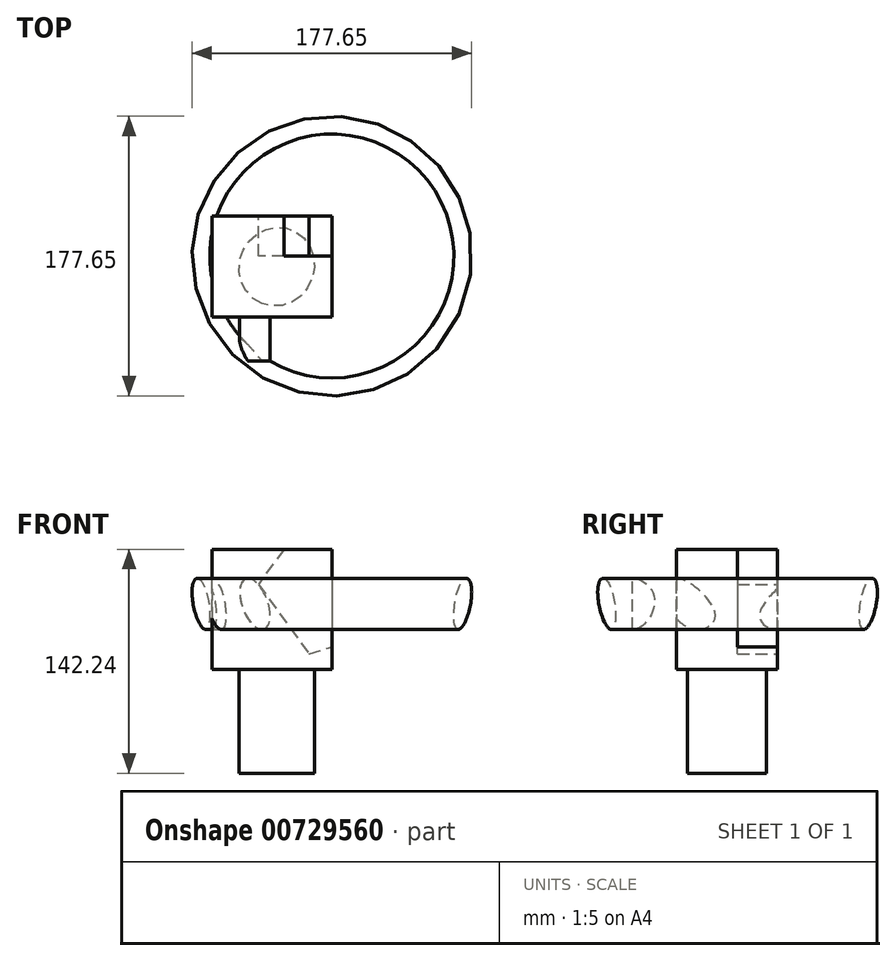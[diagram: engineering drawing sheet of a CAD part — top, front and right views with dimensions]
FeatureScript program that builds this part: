
annotation { "Feature Type Name" : "Feature", "Feature Type Description" : "" }
export const myFeature = defineFeature(function(context is Context, id is Id, definition is map)
    precondition{}
    {
        {
            var Q0;
            Q0=qCreatedBy(makeId("Front.planeOp"),FACE);
            var sketch = newSketch(context, id + "F0", { "sketchPlane" : qUnion([Q0])});
            skLineSegment(sketch, "E0", {"start": v(-41.12, 88.64) * mm, "end": v(35.08, 88.64) * mm});
            skLineSegment(sketch, "E1", {"start": v(35.08, 88.64) * mm, "end": v(35.08, 12.44) * mm});
            skLineSegment(sketch, "E2", {"start": v(35.08, 12.44) * mm, "end": v(-41.12, 12.44) * mm});
            skLineSegment(sketch, "E3", {"start": v(-41.12, 12.44) * mm, "end": v(-41.12, 88.64) * mm});
            skSolve(sketch);
        }
        {
            var Q0;
            Q0 = qSketchRegion(id + "F0", true);
            extrude(context, id + "F1", {"entities" : qUnion([Q0]), "oppositeDirection" : true, "depth" : 64.26 * mm, "offsetDistance" : 25.4 * mm});
        }
        {
            var Q0;
            Q0=makeQuery(id+"F1.opExtrude","CAP_FACE",FACE,{"disambiguationData":[OSD([sQuery(id+"F0.wireOp",EDGE,"E0"),sQuery(id+"F0.wireOp",EDGE,"E1"),sQuery(id+"F0.wireOp",EDGE,"E2"),sQuery(id+"F0.wireOp",EDGE,"E3")])],"isStart":false});
            var sketch = newSketch(context, id + "F2", { "sketchPlane" : qUnion([Q0])});
            skCircle(sketch, "E4.cCircle", {"center": v(-35.08, 66.47) * mm, "radius": 37.73 * mm, "construction": true});
            skLineSegment(sketch, "E4.0", {"start": v(-20.65, 110.82) * mm, "end": v(11.56, 66.46) * mm});
            skLineSegment(sketch, "E4.1", {"start": v(11.56, 66.46) * mm, "end": v(-20.67, 22.1) * mm});
            skLineSegment(sketch, "E4.2", {"start": v(-20.67, 22.1) * mm, "end": v(-72.81, 39.06) * mm});
            skLineSegment(sketch, "E4.3", {"start": v(-72.81, 39.06) * mm, "end": v(-72.8, 93.89) * mm});
            skLineSegment(sketch, "E4.4", {"start": v(-72.8, 93.89) * mm, "end": v(-20.65, 110.82) * mm});
            skPoint(sketch, "E4.0.midPoint", {"position": v(-4.55, 88.64) * mm});
            skSolve(sketch);
        }
        {
            var Q0;
            Q0 = qSketchRegion(id + "F2", true);
            extrude(context, id + "F3", {"entities" : qUnion([Q0]), "operationType" : NewBodyOperationType.REMOVE, "oppositeDirection" : true, "depth" : 25.4 * mm, "offsetDistance" : 25.4 * mm});
        }
        {
            var Q0;
            Q0=makeQuery(id+"F1.opExtrude","SWEPT_FACE",FACE,{"disambiguationData":[OSD([sQuery(id+"F0.wireOp",EDGE,"E2")])]});
            var sketch = newSketch(context, id + "F4", { "sketchPlane" : qUnion([Q0])});
            skEllipse(sketch, "E5", {"center": v(0, -32.13) * mm, "majorRadius": 25.18 * mm, "minorRadius": 23.75 * mm, "majorAxis": v(-0.37, 0.93)});
            skPoint(sketch, "E5.centerSnap0", {"position": v(-41.12, -32.13) * mm});
            skSolve(sketch);
        }
        {
            var Q0;
            Q0 = qSketchRegion(id + "F4", true);
            extrude(context, id + "F5", {"entities" : qUnion([Q0]), "depth" : 66.04 * mm, "offsetDistance" : 25.4 * mm});
        }
        {
            var Q0;
            Q0=makeQuery(id+"F1.opExtrude","CAP_FACE",FACE,{"disambiguationData":[OSD([sQuery(id+"F0.wireOp",EDGE,"E0"),sQuery(id+"F0.wireOp",EDGE,"E1"),sQuery(id+"F0.wireOp",EDGE,"E2"),sQuery(id+"F0.wireOp",EDGE,"E3")])],"isStart":true});
            var sketch = newSketch(context, id + "F6", { "sketchPlane" : qUnion([Q0])});
            skEllipse(sketch, "E6", {"center": v(-13.82, 53.97) * mm, "majorRadius": 17 * mm, "minorRadius": 8.18 * mm, "majorAxis": v(-0.34, 0.94)});
            skSolve(sketch);
        }
        {
            var Q0;
            Q0 = qSketchRegion(id + "F6", true);
            extrude(context, id + "F7", {"entities" : qUnion([Q0]), "operationType" : NewBodyOperationType.ADD, "depth" : 27.94 * mm, "offsetDistance" : 25.4 * mm});
        }
        {
            var Q0;
            Q0=makeQuery(id+"F7.opExtrude","CAP_FACE",FACE,{"disambiguationData":[OSD([sQuery(id+"F6.wireOp",EDGE,"E6")])],"isStart":false});
            var Q1;
            Q1=makeQuery(id+"F3.boolean.opBoolean","INTERSECT",EDGE,{"derivedFrom":[makeQuery(id+"F1.opExtrude","SWEPT_FACE",FACE,{"disambiguationData":[OSD([sQuery(id+"F0.wireOp",EDGE,"E1")])]}),makeQuery(id+"F3.opExtrude","CAP_FACE",FACE,{"disambiguationData":[OSD([sQuery(id+"F2.wireOp",EDGE,"E4.0"),sQuery(id+"F2.wireOp",EDGE,"E4.1"),sQuery(id+"F2.wireOp",EDGE,"E4.2"),sQuery(id+"F2.wireOp",EDGE,"E4.3"),sQuery(id+"F2.wireOp",EDGE,"E4.4")])],"isStart":false})]});
            revolve(context, id + "F8", {"operationType" : NewBodyOperationType.ADD, "surfaceOperationType" : NewSurfaceOperationType.NEW, "entities" : qUnion([Q0]), "axis" : qUnion([Q1]), "revolveType" : RevolveType.FULL});
        }
    });
